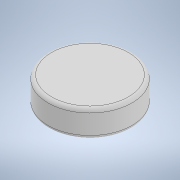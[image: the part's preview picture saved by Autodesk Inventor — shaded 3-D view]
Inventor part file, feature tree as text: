
AUTODESK INVENTOR PART (.ipt)
format: ipt  version: 2021.1 (Build 251245000, 245)  size: 119,296 bytes
history: native  units: in
note: dims shown in document units (in); Inventor stores cm internally (conversion verified against a paired STEP export)
features: extrude x1, fillet x1, sketch x1
ambient origin geometry x8: Origin, YZ Plane, XZ Plane, XY Plane, X Axis, Y Axis, Z Axis, Center Point
bodies: Solid1 (feature_tree)
feature tree (3):
  extrude  "Extrusion1"  Depth=0.375in TaperAngle=0.0deg
  fillet  "Fillet1"  Radius=0.05in
  sketch  "Sketch1"  dims[d0=1.185in d1=0.375in d2=0.0in d3=0.05in]
